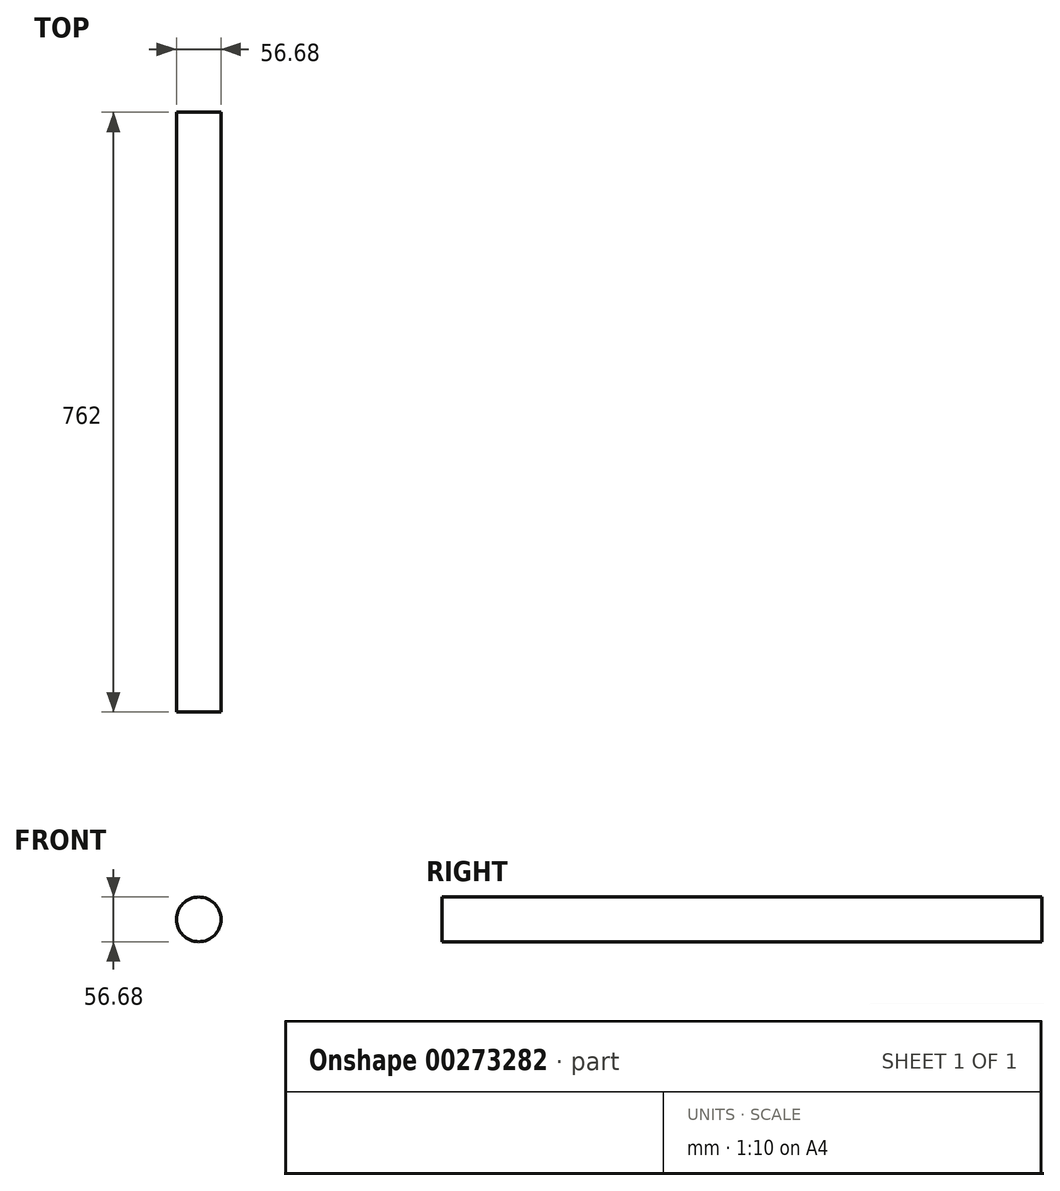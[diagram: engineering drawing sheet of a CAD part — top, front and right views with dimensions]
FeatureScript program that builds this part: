
annotation { "Feature Type Name" : "Feature", "Feature Type Description" : "" }
export const myFeature = defineFeature(function(context is Context, id is Id, definition is map)
    precondition{}
    {
        {
            var Q0;
            Q0=qCreatedBy(makeId("Front.planeOp"),FACE);
            var sketch = newSketch(context, id + "F0", { "sketchPlane" : qUnion([Q0])});
            skCircle(sketch, "E0", {"center": v(0, 0) * mm, "radius": 28.34 * mm});
            skSolve(sketch);
        }
        {
            var Q0;
            Q0 = qSketchRegion(id + "F0", true);
            extrude(context, id + "F1", {"entities" : qUnion([Q0]), "depth" : 762 * mm});
        }
    });
